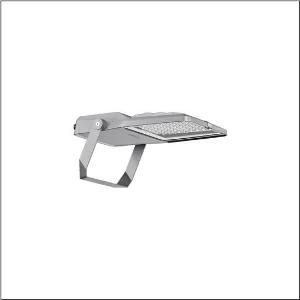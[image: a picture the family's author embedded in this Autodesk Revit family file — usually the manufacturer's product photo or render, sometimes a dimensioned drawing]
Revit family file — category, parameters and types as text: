
# Revit family: floodlight_fl_21_iq_mini___pl43_5xa7772d1a1a_00f7
name_source: partatom
category: Lighting Fixtures
units: mm (PartAtom-declared; Revit-internal decimal feet)

## family parameters
Cut with Voids When Loaded = No
Host = Face
Light Source = No
Part Type = Normal
Room Calculation Point = No
Round Connector Dimension = Use Diameter
Shared = No

## types (1)
- --- (1 x LED, 15140 lm, 143 W, 2200K)
    Apparent Load = 143 VA
    CIE Flux Codes = 27 78 99 100 100
    Color Rendering = 70
    Color Temperature = 2200K
    Default Elevation = 1800 mm
    Description = Floodlight FL 21 iQ mini, floodlight, primary light control with lens, of PMMA, primary optical cover: protective disc, of toughened safety glass, transparent, light distribution: PL43, light emission: direct distribution, installation type: surface-mounted, LED, High Power LED, rated luminous flux: 15.140lm, luminous efficacy: 106lm/W, light colour: 722, colour temperature: 2200K, control: Street-Remote, Auto-Match, Temp-Guard, Night-Set, Smart-Wire, Desk-Remote (wireless, voltage-free reading and setting of iQ features in the workshop via application-optimized NFC function/RFID function), optimised constant luminous flux control (CLO 2.0), with terminal, 6-pole, mains connection: 220..240V, AC, 50/60Hz, start of lifetime: 143W, end of service life: 152W, reduction: 61W, luminaire housing, of diecast aluminium, powder-coated, Siteco® metallic grey (DB 702S), corrosivity category C5 mid according to DIN EN ISO 12944, sealing non-destructively replaceable, mounting bracket, of steel, galvanised, powder-coated, Siteco® metallic grey (DB 702S), protection rating (complete): IP66, insulation class (complete): insulation class II (safety insulation), certification: CE, ENEC, VDE, protection symbol: D, impact resistance: IK08, permissible operating ambient temperature: -40..+40°C, permissible operating ambient temperature for outdoor applications: -40..+50°C, standard: DIN EN 12944, LABS conformity tested according to VDMA 24364:2018-05, packaging unit: 1 piece

Light Distribution: PL43
    Height = 70 mm
    Lamp = 1 x LED
    Lamp Light Flux = 15140 lm
    Lamp Power = 143 W
    Lamp count = 1
    Length = 485 mm
    Luminous efficacy = 106 lm/W
    Manufacturer = Siteco
    ModVariant = No
    Model = 5XA7772D1A1A
    Number of Poles = 1
    OnlyDefault = Yes
    Power Factor = 1
    Product Name = Floodlight FL 21 iQ mini | PL43
    Product group = floodlight | pylon annexe
    ProductGroupID = 6200
    Protection Class = Protection class II
    Protection Degree = IP 66
    RLX_Detail_Level = 1
    RLX_Emergency_Light_Flux = 0 lm
    RLX_Emergency_Type = 0
    RLX_Emergency_Type_DB = No
    RlxData = <blob elided: 96413 chars, md5=6c828b3b>
    Socket = socket
    Standby Power = 0 W
    System Light Flux = 15140 lm
    System Power = 143 W
    Type Comments = factory setting: luminous flux: 100 % | dim-lin: 254 | 730 mA
    Type Image = l_1006845.jpg
    URL = http://relux.com
    VarID = @adj_111867
    Voltage = 0 V
    Weight = 0.00 kg
    Width = 337 mm

## geometry (parser evidence)
native form markers: Blend x4, Sweep x11
no freeform markers — native parametric forms only
